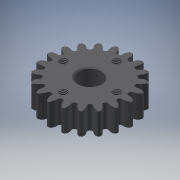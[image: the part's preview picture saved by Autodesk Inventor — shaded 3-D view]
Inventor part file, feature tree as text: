
AUTODESK INVENTOR PART (.ipt)
format: ipt  version: 2016 (Build 200138000, 138)  size: 660,480 bytes
history: native  units: mm
features: other x14, thread x4, sketch x4, revolve x3, extrude x2, hole x1
ambient origin geometry x8: Origin, YZ Plane, XZ Plane, XY Plane, X Axis, Y Axis, Z Axis, Center Point
bodies: Solid1 (feature_tree)
feature tree (28):
  revolve  "Revolution1"  [1 undecoded]
  extrude  "Extrusion1"  TaperAngle=360.0deg  [1 undecoded]
  hole  "Hole1"  [1 undecoded]
  revolve  "Revolution2"  [1 undecoded]
  revolve  "Revolution3"  [1 undecoded]
  other  "b_XY"
  other  "b_YZ"
  other  "b_ZX"
  other  "b_X"
  other  "b_Y"
  other  "b_Z"
  other  "b_Center"
  other  "turn_around_XY"
  other  "turn_around_YZ"
  other  "turn_around_ZX"
  other  "turn_around_X"
  other  "turn_around_Y"
  other  "turn_around_Z"
  other  "turn_around_Center"
  extrude  "押し出し2"  Depth=10.0mm TaperAngle=360.0deg
  thread  "ねじ1"
  thread  "ねじ2"
  thread  "ねじ3"
  thread  "ねじ4"
  sketch  "Sketch_12"  dims[d11=360.0deg d12=0.0mm d13=7.0mm d14=2.0mm d15=40.0mm d17=360.0deg d19=6.0mm d20=0.0mm d21=10.0mm d22=0.0mm d23=10.0mm d24=0.0mm d25=10.0mm d26=0.0mm d27=10.0mm d28=0.0mm]
  sketch  "Sketch_3"  dims[d0=360.0deg d1=6.0mm d2=0.0mm]
  sketch  "Sketch3"  dims[d3=6.0mm d4=6.0mm d5=4.0mm d6=2.0mm d7=90.0deg d8=6.0mm d9=0.0mm d10=360.0deg]
  sketch  "スケッチ6"
note: 5 required parameter values undecoded (feature->parameter linkage not recoverable at this tier; creation-order binding heuristic only, values carry confidence <= 0.55)